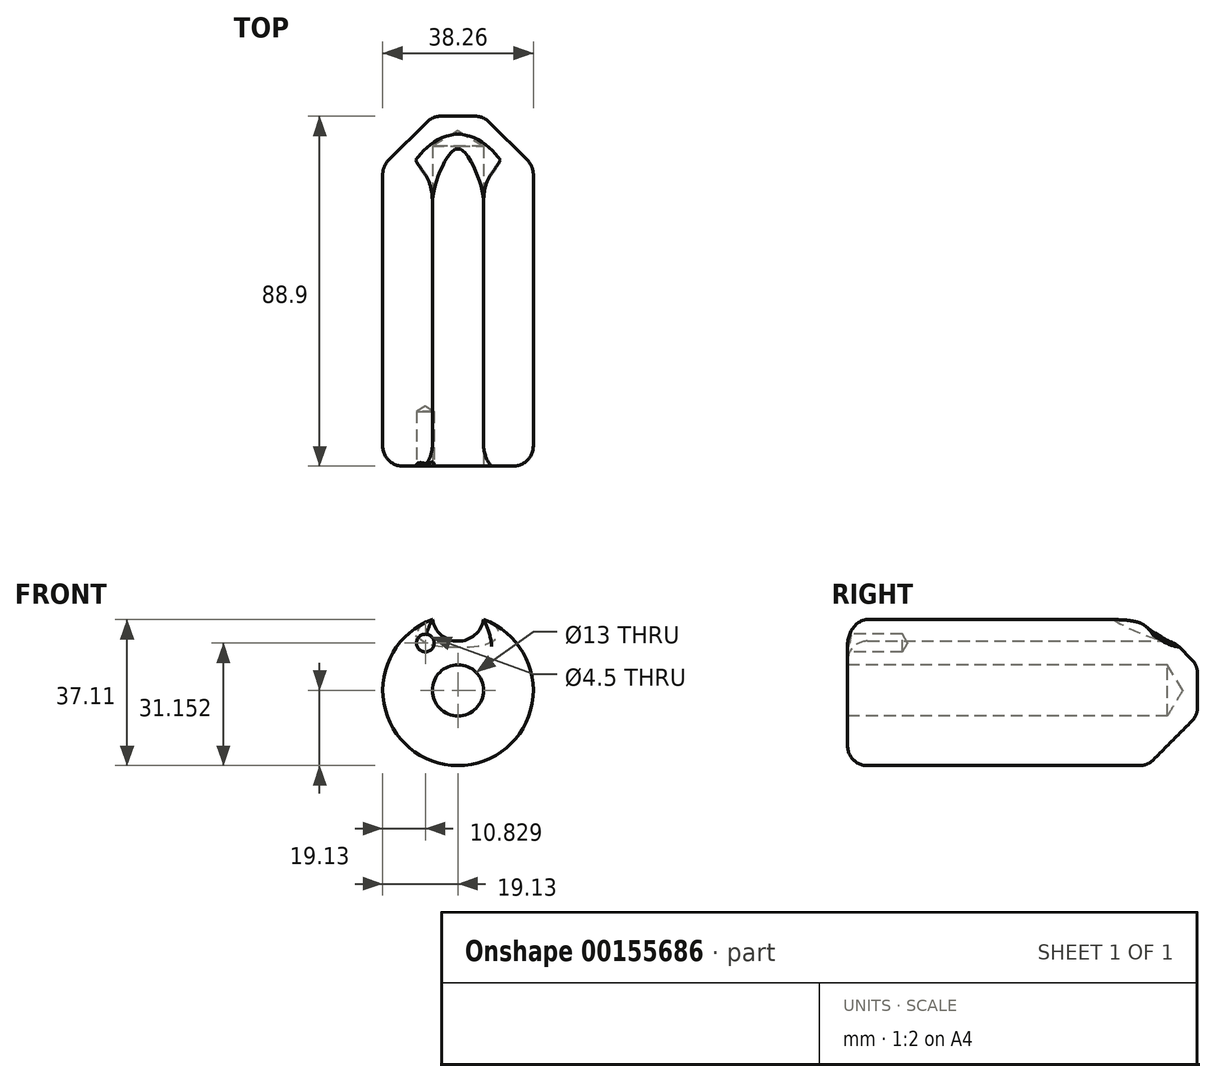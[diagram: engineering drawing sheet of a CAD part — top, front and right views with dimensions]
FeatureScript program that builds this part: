
annotation { "Feature Type Name" : "Feature", "Feature Type Description" : "" }
export const myFeature = defineFeature(function(context is Context, id is Id, definition is map)
    precondition{}
    {
        {
            var Q0;
            Q0=qCreatedBy(makeId("Front.planeOp"),FACE);
            var sketch = newSketch(context, id + "F0", { "sketchPlane" : qUnion([Q0])});
            skArc(sketch, "E0", {"start": v(-6.52, 17.98) * mm, "mid": v(0, -19.13) * mm, "end": v(6.52, 17.98) * mm});
            skCircle(sketch, "E1", {"center": v(0, 0) * mm, "radius": 6.5 * mm});
            skLineSegment(sketch, "E2", {"start": v(0, 6.5) * mm, "end": v(0, 12.5) * mm, "construction": true});
            skArc(sketch, "E3", {"start": v(-6.52, 17.98) * mm, "mid": v(0, 12.5) * mm, "end": v(6.52, 17.98) * mm});
            skSolve(sketch);
        }
        {
            var Q0;
            Q0 = qSketchRegion(id + "F0", true);
            var Q1;
            Q1=makeQuery(id+"F0.imprint","IMPRINT",FACE,{"disambiguationData":[TD([[makeQuery(id+"F0.imprint","IMPRINT",EDGE,{"derivedFrom":sQuery(id+"F0.wireOp",EDGE,"E1")}),1.0]])]});
            extrude(context, id + "F1", {"entities" : qUnion([Q0, Q1]), "depth" : 88.9 * mm});
        }
        {
            var Q0;
            Q0=makeQuery(id+"F1.opExtrude","CAP_FACE",FACE,{"disambiguationData":[OSD([sQuery(id+"F0.wireOp",EDGE,"E0"),sQuery(id+"F0.wireOp",EDGE,"E3")])],"isStart":false});
            var sketch = newSketch(context, id + "F2", { "sketchPlane" : qUnion([Q0])});
            skCircle(sketch, "E4", {"center": v(0, 0) * mm, "radius": 6.5 * mm});
            skCircle(sketch, "E5", {"center": v(-8.3, 12.02) * mm, "radius": 2.3 * mm});
            skSolve(sketch);
        }
        {
            var Q0;
            Q0=sQuery(id+"F2.wireOp",VERTEX,"E4.center");
            var Q1;
            Q1=makeQuery(id+"F1.opExtrude","SWEPT_BODY",BODY,{"disambiguationData":[OSD([sQuery(id+"F0.wireOp",EDGE,"E0"),sQuery(id+"F0.wireOp",EDGE,"E3")])]});
            hole(context, id + "F3", {"style" : HoleStyle.SIMPLE, "endStyle" : HoleEndStyle.BLIND, "holeDiameter" : 13 * mm, "holeDepth" : 81.28 * mm, "locations" : qUnion([Q0]), "scope" : qUnion([Q1])});
        }
        {
            var Q0;
            Q0=sQuery(id+"F2.wireOp",VERTEX,"E5.center");
            var Q1;
            Q1=makeQuery(id+"F1.opExtrude","SWEPT_BODY",BODY,{"disambiguationData":[OSD([sQuery(id+"F0.wireOp",EDGE,"E0"),sQuery(id+"F0.wireOp",EDGE,"E3")])]});
            hole(context, id + "F4", {"style" : HoleStyle.SIMPLE, "endStyle" : HoleEndStyle.BLIND, "holeDiameter" : 4.5 * mm, "holeDepth" : 13.9 * mm, "locations" : qUnion([Q0]), "scope" : qUnion([Q1])});
        }
        {
            var Q0;
            Q0=makeQuery(id+"F1.opExtrude","CAP_EDGE",EDGE,{"disambiguationData":[OSD([sQuery(id+"F0.wireOp",EDGE,"E0")])],"isStart":true});
            chamfer(context, id + "F5", {"entities" : qUnion([Q0]), "width" : 12.7 * mm, "tangentPropagation" : true});
        }
        {
            var Q0;
            {var subQ0=sQuery(id+"F0.wireOp",EDGE,"E0");Q0=makeQuery(id+"F5.opChamfer","BLEND_EDGE",EDGE,{"blendedFrom":[makeQuery(id+"F1.opExtrude","CAP_EDGE",EDGE,{"disambiguationData":[OSD([subQ0])],"isStart":true}),makeQuery(id+"F1.opExtrude","SWEPT_FACE",FACE,{"disambiguationData":[OSD([subQ0])]})],"blendedInto":[makeQuery(id+"F1.opExtrude","SWEPT_FACE",FACE,{"disambiguationData":[OSD([subQ0])]})]});}
            var Q1;
            Q1=makeQuery(id+"F1.opExtrude","CAP_EDGE",EDGE,{"disambiguationData":[OSD([sQuery(id+"F0.wireOp",EDGE,"E0")])],"isStart":false});
            var Q2;
            Q2=makeQuery(id+"F3.hole-0.boolean.opBoolean","COPY",EDGE,{"derivedFrom":makeQuery(id+"F3.hole-0.opRevolve","SWEPT_EDGE",EDGE,{"disambiguationData":[OSD([sQuery(id+"F3.hole-0.sketch.wireOp",EDGE,"core_line_2"),sQuery(id+"F3.hole-0.sketch.wireOp",EDGE,"core_line_3")])]})});
            var Q3;
            Q3=makeQuery(id+"F1.opExtrude","CAP_EDGE",EDGE,{"disambiguationData":[OSD([sQuery(id+"F0.wireOp",EDGE,"E3")])],"isStart":false});
            var Q4;
            Q4=makeQuery(id+"F5.opChamfer","BLEND_FACE",FACE,{"disambiguationData":[OSD([sQuery(id+"F0.wireOp",EDGE,"E0")])]});
            fillet(context, id + "F6", {"entities" : qUnion([Q0, Q1, Q2, Q3, Q4]), "radius" : 5.08 * mm, "tangentPropagation" : true, "allowEdgeOverflow" : false});
        }
    });
